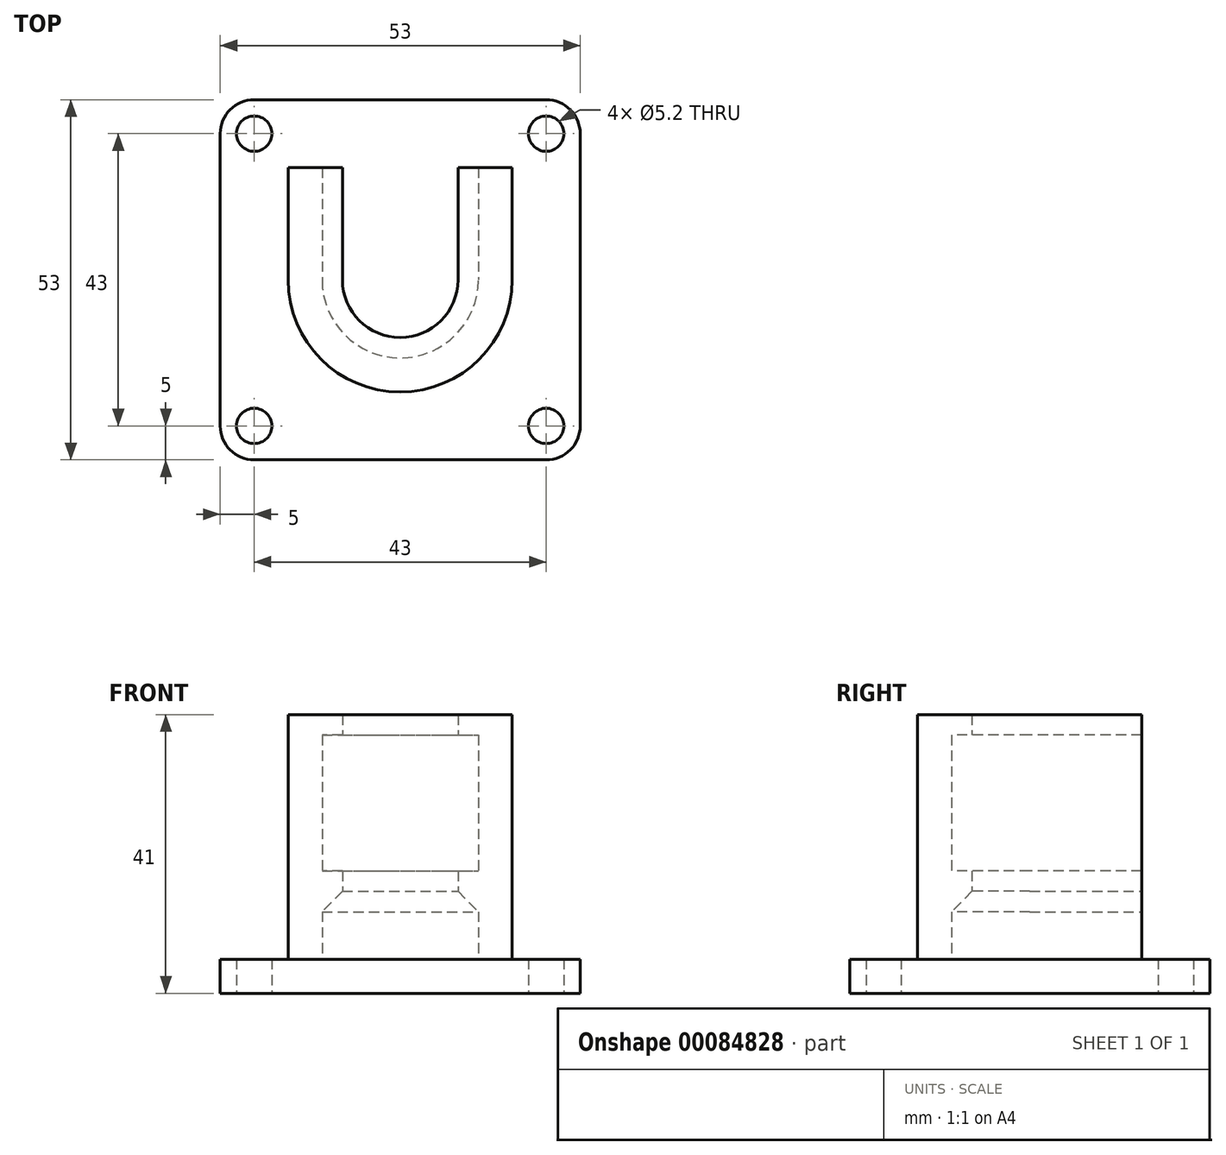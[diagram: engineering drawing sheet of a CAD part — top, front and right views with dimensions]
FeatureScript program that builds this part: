
annotation { "Feature Type Name" : "Feature", "Feature Type Description" : "" }
export const myFeature = defineFeature(function(context is Context, id is Id, definition is map)
    precondition{}
    {
        {
            var Q0;
            Q0=qCreatedBy(makeId("Top.planeOp"),FACE);
            var sketch = newSketch(context, id + "F0", { "sketchPlane" : qUnion([Q0])});
            skArc(sketch, "E0", {"start": v(-11.5, 0) * mm, "mid": v(0, -11.5) * mm, "end": v(11.5, 0) * mm});
            skArc(sketch, "E1", {"start": v(-16.5, 0) * mm, "mid": v(0, -16.5) * mm, "end": v(16.5, 0) * mm});
            skLineSegment(sketch, "E2", {"start": v(16.5, 0) * mm, "end": v(16.5, 16.5) * mm});
            skLineSegment(sketch, "E3", {"start": v(16.5, 16.5) * mm, "end": v(11.5, 16.5) * mm});
            skLineSegment(sketch, "E4", {"start": v(11.5, 16.5) * mm, "end": v(11.5, 0) * mm});
            skLineSegment(sketch, "E5", {"start": v(-16.5, 0) * mm, "end": v(-16.5, 16.5) * mm});
            skLineSegment(sketch, "E6", {"start": v(-16.5, 16.5) * mm, "end": v(-11.5, 16.5) * mm});
            skLineSegment(sketch, "E7", {"start": v(-11.5, 16.5) * mm, "end": v(-11.5, 0) * mm});
            skLineSegment(sketch, "E8.bottom", {"start": v(-21.5, 26.5) * mm, "end": v(21.5, 26.5) * mm});
            skLineSegment(sketch, "E8.top", {"start": v(-21.5, -26.5) * mm, "end": v(21.5, -26.5) * mm});
            skLineSegment(sketch, "E8.left", {"start": v(-26.5, 21.5) * mm, "end": v(-26.5, -21.5) * mm});
            skLineSegment(sketch, "E8.right", {"start": v(26.5, 21.5) * mm, "end": v(26.5, -21.5) * mm});
            skPoint(sketch, "E9", {"position": v(-26.5, 0) * mm});
            skPoint(sketch, "E10", {"position": v(0, 26.5) * mm});
            skCircle(sketch, "E11", {"center": v(-21.5, 21.5) * mm, "radius": 2.6 * mm});
            skCircle(sketch, "E12", {"center": v(-21.5, 21.5) * mm, "radius": 5 * mm});
            skCircle(sketch, "E13", {"center": v(21.5, 21.5) * mm, "radius": 2.6 * mm});
            skCircle(sketch, "E14", {"center": v(21.5, 21.5) * mm, "radius": 5 * mm});
            skCircle(sketch, "E15", {"center": v(-21.5, -21.5) * mm, "radius": 2.6 * mm});
            skCircle(sketch, "E16", {"center": v(-21.5, -21.5) * mm, "radius": 5 * mm});
            skCircle(sketch, "E17", {"center": v(21.5, -21.5) * mm, "radius": 2.6 * mm});
            skCircle(sketch, "E18", {"center": v(21.5, -21.5) * mm, "radius": 5 * mm});
            skPoint(sketch, "E19.orphan", {"position": v(-26.5, 26.5) * mm});
            skPoint(sketch, "E20.orphan", {"position": v(26.5, 26.5) * mm});
            skPoint(sketch, "E21.orphan", {"position": v(-26.5, -26.5) * mm});
            skSolve(sketch);
        }
        {
            var Q0;
            Q0=makeQuery(id+"F0.imprint","IMPRINT",FACE,{"disambiguationData":[TD([[makeQuery(id+"F0.imprint","IMPRINT",EDGE,{"derivedFrom":sQuery(id+"F0.wireOp",EDGE,"E0")}),1.0]])]});
            var Q1;
            Q1=makeQuery(id+"F0.imprint","IMPRINT",FACE,{"disambiguationData":[TD([[makeQuery(id+"F0.imprint","IMPRINT",EDGE,{"derivedFrom":sQuery(id+"F0.wireOp",EDGE,"E0")}),-1.0]])]});
            var Q2;
            Q2=makeQuery(id+"F0.imprint","IMPRINT",FACE,{"disambiguationData":[TD([[makeQuery(id+"F0.imprint","IMPRINT",EDGE,{"derivedFrom":sQuery(id+"F0.wireOp",EDGE,"E11")}),-1.0]])]});
            var Q3;
            Q3=makeQuery(id+"F0.imprint","IMPRINT",FACE,{"disambiguationData":[TD([[makeQuery(id+"F0.imprint","IMPRINT",EDGE,{"derivedFrom":sQuery(id+"F0.wireOp",EDGE,"E15")}),-1.0]])]});
            var Q4;
            Q4=makeQuery(id+"F0.imprint","IMPRINT",FACE,{"disambiguationData":[TD([[makeQuery(id+"F0.imprint","IMPRINT",EDGE,{"derivedFrom":sQuery(id+"F0.wireOp",EDGE,"E17")}),-1.0]])]});
            var Q5;
            Q5=makeQuery(id+"F0.imprint","IMPRINT",FACE,{"disambiguationData":[TD([[makeQuery(id+"F0.imprint","IMPRINT",EDGE,{"derivedFrom":sQuery(id+"F0.wireOp",EDGE,"E13")}),-1.0]])]});
            extrude(context, id + "F1", {"entities" : qUnion([Q0, Q1, Q2, Q3, Q4, Q5]), "depth" : 5 * mm});
        }
        {
            var Q0;
            Q0=makeQuery(id+"F1.opExtrude","CAP_FACE",FACE,{"disambiguationData":[OSD([sQuery(id+"F0.wireOp",EDGE,"E8.bottom"),sQuery(id+"F0.wireOp",EDGE,"E8.top"),sQuery(id+"F0.wireOp",EDGE,"E8.left"),sQuery(id+"F0.wireOp",EDGE,"E8.right"),sQuery(id+"F0.wireOp",EDGE,"E11"),sQuery(id+"F0.wireOp",EDGE,"E12"),sQuery(id+"F0.wireOp",EDGE,"E13"),sQuery(id+"F0.wireOp",EDGE,"E14"),sQuery(id+"F0.wireOp",EDGE,"E15"),sQuery(id+"F0.wireOp",EDGE,"E16"),sQuery(id+"F0.wireOp",EDGE,"E17"),sQuery(id+"F0.wireOp",EDGE,"E18")])],"isStart":false});
            var sketch = newSketch(context, id + "F2", { "sketchPlane" : qUnion([Q0])});
            skArc(sketch, "E22", {"start": v(-11.5, 0) * mm, "mid": v(0, -11.5) * mm, "end": v(11.5, 0) * mm});
            skArc(sketch, "E23", {"start": v(-16.5, 0) * mm, "mid": v(0, -16.5) * mm, "end": v(16.5, 0) * mm});
            skLineSegment(sketch, "E24", {"start": v(16.5, 0) * mm, "end": v(16.5, 16.5) * mm});
            skLineSegment(sketch, "E25", {"start": v(16.5, 16.5) * mm, "end": v(11.5, 16.5) * mm});
            skLineSegment(sketch, "E26", {"start": v(11.5, 16.5) * mm, "end": v(11.5, 0) * mm});
            skLineSegment(sketch, "E27", {"start": v(-16.5, 0) * mm, "end": v(-16.5, 16.5) * mm});
            skLineSegment(sketch, "E28", {"start": v(-16.5, 16.5) * mm, "end": v(-11.5, 16.5) * mm});
            skLineSegment(sketch, "E29", {"start": v(-11.5, 16.5) * mm, "end": v(-11.5, 0) * mm});
            skLineSegment(sketch, "E30.bottom", {"start": v(-21.5, 26.5) * mm, "end": v(21.5, 26.5) * mm});
            skLineSegment(sketch, "E30.top", {"start": v(-21.5, -26.5) * mm, "end": v(21.5, -26.5) * mm});
            skLineSegment(sketch, "E30.left", {"start": v(-26.5, 21.5) * mm, "end": v(-26.5, -21.5) * mm});
            skLineSegment(sketch, "E30.right", {"start": v(26.5, 21.5) * mm, "end": v(26.5, -21.5) * mm});
            skPoint(sketch, "E31", {"position": v(-26.5, 0) * mm});
            skPoint(sketch, "E32", {"position": v(0, 26.5) * mm});
            skCircle(sketch, "E33", {"center": v(-21.5, 21.5) * mm, "radius": 2.6 * mm});
            skCircle(sketch, "E34", {"center": v(-21.5, 21.5) * mm, "radius": 5 * mm});
            skCircle(sketch, "E35", {"center": v(21.5, 21.5) * mm, "radius": 2.6 * mm});
            skCircle(sketch, "E36", {"center": v(21.5, 21.5) * mm, "radius": 5 * mm});
            skCircle(sketch, "E37", {"center": v(-21.5, -21.5) * mm, "radius": 2.6 * mm});
            skCircle(sketch, "E38", {"center": v(-21.5, -21.5) * mm, "radius": 5 * mm});
            skCircle(sketch, "E39", {"center": v(21.5, -21.5) * mm, "radius": 2.6 * mm});
            skCircle(sketch, "E40", {"center": v(21.5, -21.5) * mm, "radius": 5 * mm});
            skPoint(sketch, "E41.orphan", {"position": v(-26.5, 26.5) * mm});
            skPoint(sketch, "E42.orphan", {"position": v(26.5, 26.5) * mm});
            skPoint(sketch, "E43.orphan", {"position": v(-26.5, -26.5) * mm});
            skSolve(sketch);
        }
        {
            var Q0;
            Q0=makeQuery(id+"F2.imprint","IMPRINT",FACE,{"disambiguationData":[TD([[makeQuery(id+"F2.imprint","IMPRINT",EDGE,{"derivedFrom":sQuery(id+"F2.wireOp",EDGE,"E22")}),-1.0]])]});
            extrude(context, id + "F3", {"entities" : qUnion([Q0]), "operationType" : NewBodyOperationType.ADD, "depth" : 36 * mm});
        }
        {
            var Q0;
            Q0=makeQuery(id+"F1.opExtrude","CAP_FACE",FACE,{"disambiguationData":[OSD([sQuery(id+"F0.wireOp",EDGE,"E8.bottom"),sQuery(id+"F0.wireOp",EDGE,"E8.top"),sQuery(id+"F0.wireOp",EDGE,"E8.left"),sQuery(id+"F0.wireOp",EDGE,"E8.right"),sQuery(id+"F0.wireOp",EDGE,"E11"),sQuery(id+"F0.wireOp",EDGE,"E12"),sQuery(id+"F0.wireOp",EDGE,"E13"),sQuery(id+"F0.wireOp",EDGE,"E14"),sQuery(id+"F0.wireOp",EDGE,"E15"),sQuery(id+"F0.wireOp",EDGE,"E16"),sQuery(id+"F0.wireOp",EDGE,"E17"),sQuery(id+"F0.wireOp",EDGE,"E18")])],"isStart":false});
            cPlane(context, id + "F4", {"entities" : qUnion([Q0]), "cplaneType" : CPlaneType.OFFSET, "offset" : 10 * mm, "width" : 150 * mm, "height" : 150 * mm});
        }
        {
            var Q0;
            Q0=qCreatedBy(id+"F4.planeOp",FACE);
            var sketch = newSketch(context, id + "F5", { "sketchPlane" : qUnion([Q0])});
            skArc(sketch, "E44", {"start": v(-11.5, 0) * mm, "mid": v(0, -11.5) * mm, "end": v(11.5, 0) * mm});
            skArc(sketch, "E45", {"start": v(-8.5, 0) * mm, "mid": v(0, -8.5) * mm, "end": v(8.5, 0) * mm});
            skLineSegment(sketch, "E46", {"start": v(-8.5, 0) * mm, "end": v(-8.5, 16.5) * mm});
            skLineSegment(sketch, "E47", {"start": v(-8.5, 16.5) * mm, "end": v(-11.5, 16.5) * mm});
            skLineSegment(sketch, "E48", {"start": v(-11.5, 16.5) * mm, "end": v(-11.5, 0) * mm});
            skLineSegment(sketch, "E49", {"start": v(8.5, 0) * mm, "end": v(8.5, 16.5) * mm});
            skLineSegment(sketch, "E50", {"start": v(8.5, 16.5) * mm, "end": v(11.5, 16.5) * mm});
            skLineSegment(sketch, "E51", {"start": v(11.5, 16.5) * mm, "end": v(11.5, 0) * mm});
            skSolve(sketch);
        }
        {
            var Q0;
            Q0=makeQuery(id+"F5.imprint","IMPRINT",FACE,{"disambiguationData":[TD([[makeQuery(id+"F5.imprint","IMPRINT",EDGE,{"derivedFrom":sQuery(id+"F5.wireOp",EDGE,"E44")}),1.0]])]});
            extrude(context, id + "F6", {"entities" : qUnion([Q0]), "operationType" : NewBodyOperationType.ADD, "depth" : 3 * mm});
        }
        {
            var Q0;
            Q0=makeQuery(id+"F6.opExtrude","CAP_FACE",FACE,{"disambiguationData":[OSD([sQuery(id+"F5.wireOp",EDGE,"E44"),sQuery(id+"F5.wireOp",EDGE,"E45"),sQuery(id+"F5.wireOp",EDGE,"E46"),sQuery(id+"F5.wireOp",EDGE,"E47"),sQuery(id+"F5.wireOp",EDGE,"E48"),sQuery(id+"F5.wireOp",EDGE,"E49"),sQuery(id+"F5.wireOp",EDGE,"E50"),sQuery(id+"F5.wireOp",EDGE,"E51")])],"isStart":false});
            cPlane(context, id + "F7", {"entities" : qUnion([Q0]), "cplaneType" : CPlaneType.OFFSET, "offset" : 20 * mm, "width" : 150 * mm, "height" : 150 * mm});
        }
        {
            var Q0;
            Q0=qCreatedBy(id+"F7.planeOp",FACE);
            var sketch = newSketch(context, id + "F8", { "sketchPlane" : qUnion([Q0])});
            skArc(sketch, "E52", {"start": v(-11.5, 0) * mm, "mid": v(0, -11.5) * mm, "end": v(11.5, 0) * mm});
            skArc(sketch, "E53", {"start": v(-8.5, 0) * mm, "mid": v(0, -8.5) * mm, "end": v(8.5, 0) * mm});
            skLineSegment(sketch, "E54", {"start": v(-8.5, 0) * mm, "end": v(-8.5, 16.5) * mm});
            skLineSegment(sketch, "E55", {"start": v(-8.5, 16.5) * mm, "end": v(-11.5, 16.5) * mm});
            skLineSegment(sketch, "E56", {"start": v(-11.5, 16.5) * mm, "end": v(-11.5, 0) * mm});
            skLineSegment(sketch, "E57", {"start": v(8.5, 0) * mm, "end": v(8.5, 16.5) * mm});
            skLineSegment(sketch, "E58", {"start": v(8.5, 16.5) * mm, "end": v(11.5, 16.5) * mm});
            skLineSegment(sketch, "E59", {"start": v(11.5, 16.5) * mm, "end": v(11.5, 0) * mm});
            skSolve(sketch);
        }
        {
            var Q0;
            Q0=makeQuery(id+"F8.imprint","IMPRINT",FACE,{"disambiguationData":[TD([[makeQuery(id+"F8.imprint","IMPRINT",EDGE,{"derivedFrom":sQuery(id+"F8.wireOp",EDGE,"E52")}),1.0]])]});
            extrude(context, id + "F9", {"entities" : qUnion([Q0]), "operationType" : NewBodyOperationType.ADD, "depth" : 3 * mm});
        }
        {
            var Q0;
            Q0=makeQuery(id+"F9.opExtrude","CAP_EDGE",EDGE,{"disambiguationData":[OSD([sQuery(id+"F8.wireOp",EDGE,"E56")])],"isStart":true});
            var Q1;
            Q1=makeQuery(id+"F6.opExtrude","CAP_EDGE",EDGE,{"disambiguationData":[OSD([sQuery(id+"F5.wireOp",EDGE,"E48")])],"isStart":true});
            chamfer(context, id + "F10", {"entities" : qUnion([Q0, Q1]), "width" : 3 * mm, "tangentPropagation" : true});
        }
    });
